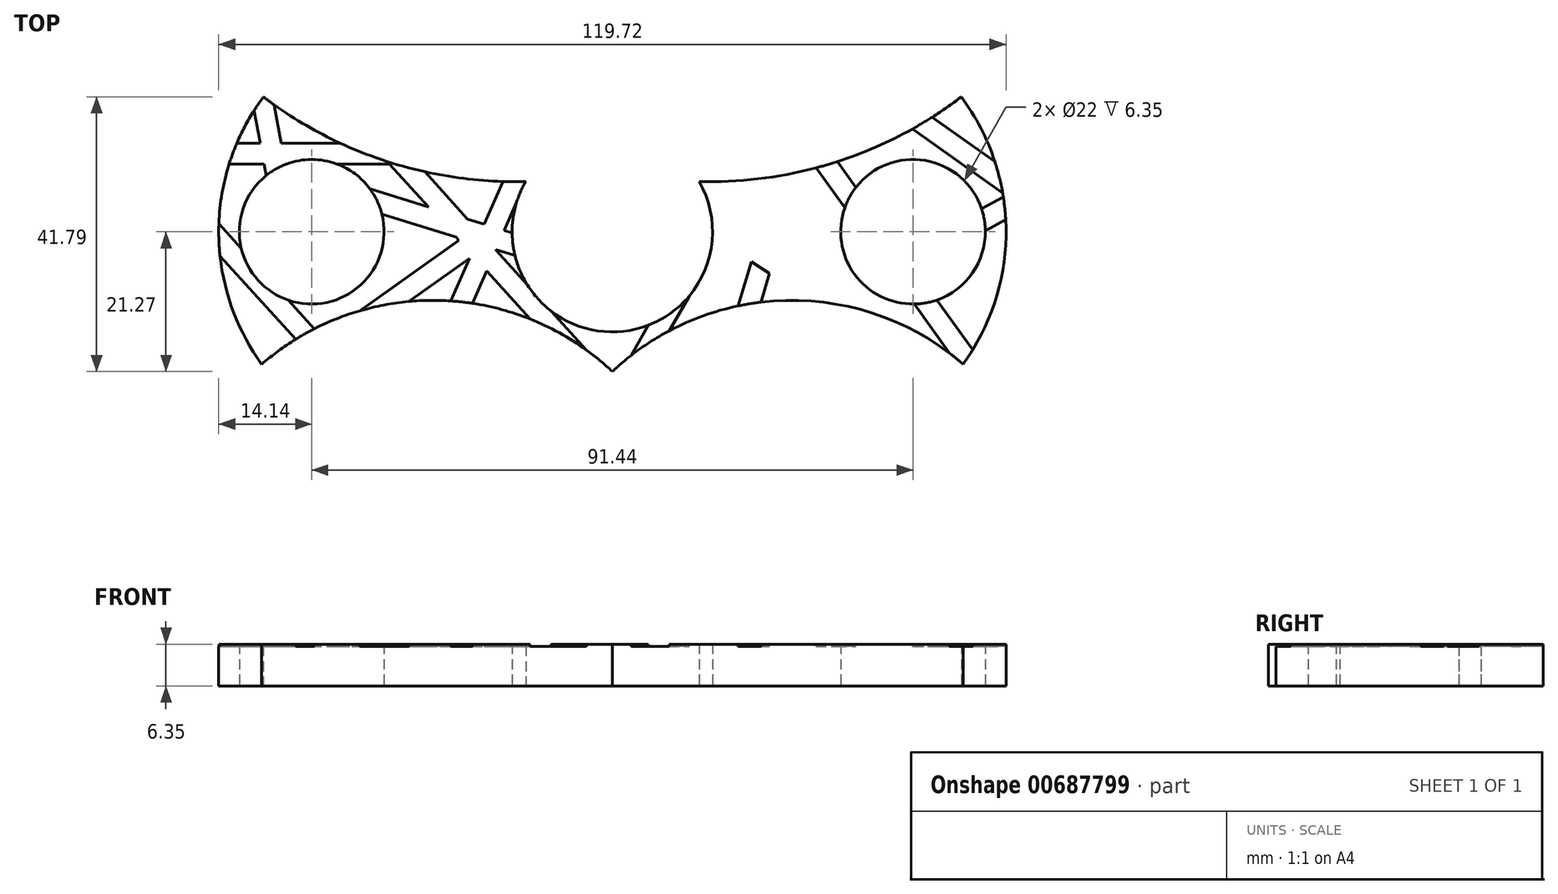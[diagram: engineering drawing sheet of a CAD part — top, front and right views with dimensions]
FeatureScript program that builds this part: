
annotation { "Feature Type Name" : "Feature", "Feature Type Description" : "" }
export const myFeature = defineFeature(function(context is Context, id is Id, definition is map)
    precondition{}
    {
        {
            assignVariable(context, id + "F0", {"name" : "thickness", "anyValue" : 6.35 * mm});
        }
        {
            var Q0;
            Q0=qCreatedBy(makeId("Top.planeOp"),FACE);
            var sketch = newSketch(context, id + "F1", { "sketchPlane" : qUnion([Q0])});
            skCircle(sketch, "E0", {"center": v(0, 0) * mm, "radius": 11 * mm});
            skCircle(sketch, "E1", {"center": v(0, 0) * mm, "radius": 63.5 * mm, "construction": true});
            skCircle(sketch, "E2", {"center": v(0, 0) * mm, "radius": 15.24 * mm});
            skLineSegment(sketch, "E3", {"start": v(0, 0) * mm, "end": v(45.72, 0) * mm, "construction": true});
            skCircle(sketch, "E4", {"center": v(45.72, 0) * mm, "radius": 11 * mm});
            skLineSegment(sketch, "E5", {"start": v(0, 0) * mm, "end": v(-45.72, 0) * mm, "construction": true});
            skCircle(sketch, "E6", {"center": v(-45.72, 0) * mm, "radius": 11 * mm});
            skLineSegment(sketch, "E7", {"start": v(0, -21.27) * mm, "end": v(3.96, -14.72) * mm});
            skLineSegment(sketch, "E8", {"start": v(0, -21.27) * mm, "end": v(-3.96, -14.72) * mm});
            skLineSegment(sketch, "E9", {"start": v(-12.5, 16.99) * mm, "end": v(-8.16, 12.87) * mm});
            skLineSegment(sketch, "E10", {"start": v(-12.5, 16.99) * mm, "end": v(-13.18, 7.66) * mm});
            skLineSegment(sketch, "E11.MirrorCS", {"start": v(12.5, 16.99) * mm, "end": v(13.18, 7.66) * mm});
            skLineSegment(sketch, "E12.MirrorCS", {"start": v(12.5, 16.99) * mm, "end": v(8.16, 12.87) * mm});
            skPoint(sketch, "E13.first.point", {"position": v(-45.72, 18.86) * mm});
            skPoint(sketch, "E13.second.point", {"position": v(-73.63, 0) * mm});
            skPoint(sketch, "E13.third.point", {"position": v(-45.72, -18.86) * mm});
            skLineSegment(sketch, "E14", {"start": v(-51.18, 0) * mm, "end": v(-51.18, -20.99) * mm, "construction": true});
            skArc(sketch, "E15", {"start": v(-53.06, 20.52) * mm, "mid": v(-34.22, 10.68) * mm, "end": v(-13.18, 7.66) * mm});
            skArc(sketch, "E16", {"start": v(-53.06, 20.52) * mm, "mid": v(-59.86, 0.23) * mm, "end": v(-53.32, -20.15) * mm});
            skPoint(sketch, "E16.second.point", {"position": v(-59.86, 0) * mm});
            skPoint(sketch, "E16.third.point", {"position": v(-56.47, -14.88) * mm});
            skArc(sketch, "E17", {"start": v(0, -21.27) * mm, "mid": v(-26.45, -10.45) * mm, "end": v(-53.32, -20.15) * mm});
            skPoint(sketch, "E18.MirrorP", {"position": v(45.72, 18.86) * mm});
            skPoint(sketch, "E19.MirrorP", {"position": v(45.72, -18.86) * mm});
            skLineSegment(sketch, "E20.MirrorCS", {"start": v(51.18, 0) * mm, "end": v(51.18, -20.99) * mm, "construction": true});
            skArc(sketch, "E21.MirrorCS", {"start": v(53.06, 20.52) * mm, "mid": v(59.86, 0.23) * mm, "end": v(53.32, -20.15) * mm});
            skPoint(sketch, "E22.MirrorP", {"position": v(56.47, -14.88) * mm});
            skArc(sketch, "E23.MirrorCS", {"start": v(0, -21.27) * mm, "mid": v(26.45, -10.45) * mm, "end": v(53.32, -20.15) * mm});
            skPoint(sketch, "E24.MirrorP", {"position": v(59.86, 0) * mm});
            skArc(sketch, "E25.MirrorCS", {"start": v(53.06, 20.52) * mm, "mid": v(34.22, 10.68) * mm, "end": v(13.18, 7.66) * mm});
            skSolve(sketch);
        }
        {
            var Q0;
            Q0=makeQuery(id+"F1.imprint","IMPRINT",FACE,{"disambiguationData":[TD([[makeQuery(id+"F1.imprint","IMPRINT",EDGE,{"derivedFrom":sQuery(id+"F1.wireOp",EDGE,"E6")}),-1.0]])]});
            var Q1;
            {var subQ0=sQuery(id+"F1.wireOp",EDGE,"E9");Q1=makeQuery(id+"F1.imprint","IMPRINT",FACE,{"disambiguationData":[TD([[makeQuery(id+"F1.imprint","IMPRINT",EDGE,{"derivedFrom":subQ0}),-1.0]])]});}
            var Q2;
            {var subQ0=sQuery(id+"F1.wireOp",EDGE,"E11.MirrorCS");Q2=makeQuery(id+"F1.imprint","IMPRINT",FACE,{"disambiguationData":[TD([[makeQuery(id+"F1.imprint","IMPRINT",EDGE,{"derivedFrom":subQ0}),-1.0]])]});}
            var Q3;
            {var subQ0=sQuery(id+"F1.wireOp",EDGE,"E7");Q3=makeQuery(id+"F1.imprint","IMPRINT",FACE,{"disambiguationData":[TD([[makeQuery(id+"F1.imprint","IMPRINT",EDGE,{"derivedFrom":subQ0}),1.0]])]});}
            var Q4;
            Q4=makeQuery(id+"F1.imprint","IMPRINT",FACE,{"disambiguationData":[TD([[makeQuery(id+"F1.imprint","IMPRINT",EDGE,{"derivedFrom":sQuery(id+"F1.wireOp",EDGE,"E0")}),1.0]])]});
            var Q5;
            {var subQ1=sQuery(id+"F1.wireOp",EDGE,"E7");Q5=makeQuery(id+"F1.imprint","IMPRINT",FACE,{"disambiguationData":[TD([[makeQuery(id+"F1.imprint","IMPRINT",EDGE,{"derivedFrom":subQ1}),-1.0]])]});}
            extrude(context, id + "F2", {"entities" : qUnion([Q0, Q1, Q2, Q3, Q4, Q5]), "depth" : getVariable(context, 'thickness'), "offsetDistance" : 25.4 * mm});
        }
        {
            var Q0;
            Q0=qCreatedBy(makeId("Top.planeOp"),FACE);
            cPlane(context, id + "F3", {"entities" : qUnion([Q0]), "cplaneType" : CPlaneType.OFFSET, "offset" : getVariable(context, 'thickness') / 2, "width" : 152.4 * mm, "height" : 152.4 * mm});
        }
        {
            var Q0;
            Q0=makeQuery(id+"F2.opExtrude","SWEPT_BODY",BODY,{"disambiguationData":[OSD([sQuery(id+"F1.wireOp",EDGE,"E6"),sQuery(id+"F1.wireOp",EDGE,"E9"),sQuery(id+"F1.wireOp",EDGE,"E10"),sQuery(id+"F1.wireOp",EDGE,"E15"),sQuery(id+"F1.wireOp",EDGE,"E16"),sQuery(id+"F1.wireOp",EDGE,"E17"),sQuery(id+"F1.wireOp",EDGE,"E11.MirrorCS"),sQuery(id+"F1.wireOp",EDGE,"E2"),sQuery(id+"F1.wireOp",EDGE,"E4"),sQuery(id+"F1.wireOp",EDGE,"E12.MirrorCS"),sQuery(id+"F1.wireOp",EDGE,"E21.MirrorCS"),sQuery(id+"F1.wireOp",EDGE,"E0"),sQuery(id+"F1.wireOp",EDGE,"E23.MirrorCS"),sQuery(id+"F1.wireOp",EDGE,"E25.MirrorCS")])]});
            var Q1;
            Q1=qCreatedBy(id+"F3.planeOp",FACE);
            mirror(context, id + "F4", {"operationType" : NewBodyOperationType.INTERSECT, "entities" : qUnion([Q0]), "mirrorPlane" : qUnion([Q1])});
        }
        {
            var Q0;
            Q0=makeQuery(id+"F2.opExtrude","CAP_FACE",FACE,{"disambiguationData":[OSD([sQuery(id+"F1.wireOp",EDGE,"E6"),sQuery(id+"F1.wireOp",EDGE,"E9"),sQuery(id+"F1.wireOp",EDGE,"E10"),sQuery(id+"F1.wireOp",EDGE,"E15"),sQuery(id+"F1.wireOp",EDGE,"E16"),sQuery(id+"F1.wireOp",EDGE,"E17"),sQuery(id+"F1.wireOp",EDGE,"E11.MirrorCS"),sQuery(id+"F1.wireOp",EDGE,"E2"),sQuery(id+"F1.wireOp",EDGE,"E4"),sQuery(id+"F1.wireOp",EDGE,"E12.MirrorCS"),sQuery(id+"F1.wireOp",EDGE,"E21.MirrorCS"),sQuery(id+"F1.wireOp",EDGE,"E0"),sQuery(id+"F1.wireOp",EDGE,"E23.MirrorCS"),sQuery(id+"F1.wireOp",EDGE,"E25.MirrorCS")])],"isStart":false});
            var sketch = newSketch(context, id + "F5", { "sketchPlane" : qUnion([Q0])});
            skLineSegment(sketch, "E26", {"start": v(-54.49, 18.45) * mm, "end": v(-53.56, 13.5) * mm});
            skLineSegment(sketch, "E27", {"start": v(-51.42, 19.31) * mm, "end": v(-50.33, 13.5) * mm});
            skLineSegment(sketch, "E28", {"start": v(-34.22, 10.68) * mm, "end": v(-27.97, 3.78) * mm});
            skLineSegment(sketch, "E29", {"start": v(-28.53, 9.14) * mm, "end": v(-22, 1.93) * mm});
            skLineSegment(sketch, "E30", {"start": v(-23.36, -1.3) * mm, "end": v(-38.4, -12.02) * mm});
            skLineSegment(sketch, "E31", {"start": v(-21.21, -3.67) * mm, "end": v(-30.94, -10.6) * mm});
            skLineSegment(sketch, "E32", {"start": v(-59.83, 1.25) * mm, "end": v(-45.32, -14.77) * mm});
            skLineSegment(sketch, "E33", {"start": v(-59.66, -3.67) * mm, "end": v(-48.16, -16.36) * mm});
            skLineSegment(sketch, "E34", {"start": v(-36.88, 6.55) * mm, "end": v(-27.97, 3.78) * mm});
            skLineSegment(sketch, "E35", {"start": v(-35.05, 2.65) * mm, "end": v(-23.78, -0.84) * mm});
            skLineSegment(sketch, "E36", {"start": v(2.86, -18.82) * mm, "end": v(10.74, -5.02) * mm});
            skLineSegment(sketch, "E37", {"start": v(21.84, 8.02) * mm, "end": v(17.94, 1.2) * mm});
            skLineSegment(sketch, "E38", {"start": v(10.83, 1.94) * mm, "end": v(13.68, 0.13) * mm});
            skLineSegment(sketch, "E39", {"start": v(39.33, -12.3) * mm, "end": v(36.89, -10.76) * mm});
            skLineSegment(sketch, "E40", {"start": v(10.86, -1.77) * mm, "end": v(12.8, -1.42) * mm});
            skLineSegment(sketch, "E41", {"start": v(9.69, -5.22) * mm, "end": v(10.74, -5.02) * mm});
            skLineSegment(sketch, "E42", {"start": v(48.62, 17.43) * mm, "end": v(58.15, 10.68) * mm});
            skPoint(sketch, "E42.endSnap0", {"position": v(34.22, 10.68) * mm});
            skLineSegment(sketch, "E43", {"start": v(45.64, 15.66) * mm, "end": v(59.34, 5.95) * mm});
            skLineSegment(sketch, "E44", {"start": v(30.99, 9.73) * mm, "end": v(41.35, -4.68) * mm});
            skLineSegment(sketch, "E45", {"start": v(34.22, 10.68) * mm, "end": v(44.15, -3.14) * mm});
            skLineSegment(sketch, "E46", {"start": v(-57.1, 13.5) * mm, "end": v(-53.56, 13.5) * mm});
            skPoint(sketch, "E46.startSnap0", {"position": v(-53.56, 13.5) * mm});
            skLineSegment(sketch, "E47", {"start": v(-58.27, 10.33) * mm, "end": v(-52.96, 10.33) * mm});
            skLineSegment(sketch, "E48", {"start": v(59.45, 5.3) * mm, "end": v(44.15, -3.14) * mm});
            skLineSegment(sketch, "E49", {"start": v(59.8, 1.88) * mm, "end": v(46.01, -5.73) * mm});
            skLineSegment(sketch, "E50", {"start": v(-34.42, -33.18) * mm, "end": v(-21.46, -3.4) * mm});
            skLineSegment(sketch, "E51", {"start": v(-31.26, -33.87) * mm, "end": v(-19.12, -5.99) * mm});
            skLineSegment(sketch, "E52.trimOffspring", {"start": v(-50.33, 13.5) * mm, "end": v(-41.42, 13.5) * mm});
            skLineSegment(sketch, "E53.trimOffspring", {"start": v(-52.96, 10.33) * mm, "end": v(-52.63, 8.56) * mm});
            skLineSegment(sketch, "E54.trimOffspring", {"start": v(-49.73, 10.33) * mm, "end": v(-49.72, 10.25) * mm});
            skLineSegment(sketch, "E55.trimOffspring", {"start": v(-49.73, 10.33) * mm, "end": v(-33.09, 10.33) * mm});
            skLineSegment(sketch, "E56.trimOffspring", {"start": v(-22, 1.93) * mm, "end": v(-19.47, 1.15) * mm});
            skLineSegment(sketch, "E57.trimOffspring", {"start": v(-23.78, -0.84) * mm, "end": v(-23.36, -1.3) * mm});
            skLineSegment(sketch, "E58.trimOffspring", {"start": v(-17.82, -2.7) * mm, "end": v(-3.94, -18.01) * mm});
            skLineSegment(sketch, "E59.trimOffspring", {"start": v(-19.47, 1.15) * mm, "end": v(-16.64, 7.66) * mm});
            skLineSegment(sketch, "E60.trimOffspring", {"start": v(-17.82, -2.7) * mm, "end": v(-9.69, -5.21) * mm});
            skLineSegment(sketch, "E61.trimOffspring", {"start": v(-21.46, -3.4) * mm, "end": v(-21.21, -3.67) * mm});
            skLineSegment(sketch, "E62.trimOffspring", {"start": v(-19.12, -5.99) * mm, "end": v(-12.5, -13.28) * mm});
            skLineSegment(sketch, "E63.trimOffspring", {"start": v(-17.73, -2.8) * mm, "end": v(-17.7, -2.73) * mm});
            skLineSegment(sketch, "E64.trimOffspring", {"start": v(-16.42, 0.2) * mm, "end": v(-10.9, -1.51) * mm});
            skLineSegment(sketch, "E65.trimOffspring", {"start": v(-16.42, 0.2) * mm, "end": v(-13.18, 7.66) * mm});
            skLineSegment(sketch, "E66.trimOffspring", {"start": v(15.26, 2.9) * mm, "end": v(8.16, 7.38) * mm});
            skLineSegment(sketch, "E67.trimOffspring", {"start": v(15.26, 2.9) * mm, "end": v(18, 7.71) * mm});
            skLineSegment(sketch, "E68.trimOffspring", {"start": v(14.82, -4.28) * mm, "end": v(8.66, -15.07) * mm});
            skLineSegment(sketch, "E69.trimOffspring", {"start": v(20, -0.1) * mm, "end": v(22.58, 0.37) * mm});
            skLineSegment(sketch, "E70.trimOffspring", {"start": v(19.35, -3.45) * mm, "end": v(30.65, -10.58) * mm});
            skLineSegment(sketch, "E71.trimOffspring", {"start": v(12.8, -1.42) * mm, "end": v(13.68, 0.13) * mm});
            skLineSegment(sketch, "E72.trimOffspring", {"start": v(20, -0.1) * mm, "end": v(17.94, 1.2) * mm});
            skLineSegment(sketch, "E73.trimOffspring", {"start": v(25.07, -2.4) * mm, "end": v(34.74, -0.63) * mm});
            skLineSegment(sketch, "E74.trimOffspring", {"start": v(14.82, -4.28) * mm, "end": v(19.35, -3.45) * mm});
            skLineSegment(sketch, "E75.trimOffspring", {"start": v(41.35, -4.68) * mm, "end": v(33.82, -8.83) * mm});
            skLineSegment(sketch, "E76.trimOffspring", {"start": v(43.21, -7.28) * mm, "end": v(35.8, -11.36) * mm});
            skLineSegment(sketch, "E77.trimOffspring", {"start": v(43.21, -7.28) * mm, "end": v(51.27, -18.5) * mm});
            skLineSegment(sketch, "E78.trimOffspring", {"start": v(46.01, -5.73) * mm, "end": v(54.8, -17.95) * mm});
            skLineSegment(sketch, "E79.trimOffspring", {"start": v(33.82, -8.83) * mm, "end": v(24.84, -3.16) * mm});
            skLineSegment(sketch, "E80", {"start": v(24.97, 8.45) * mm, "end": v(22.58, 0.37) * mm});
            skLineSegment(sketch, "E81", {"start": v(28.49, 9.13) * mm, "end": v(26.08, 1.01) * mm});
            skLineSegment(sketch, "E82.trimOffspring", {"start": v(26.08, 1.01) * mm, "end": v(35.05, 2.65) * mm});
            skLineSegment(sketch, "E83.trimOffspring", {"start": v(21.11, -4.56) * mm, "end": v(19.12, -11.28) * mm});
            skLineSegment(sketch, "E84.trimOffspring", {"start": v(25.07, -2.4) * mm, "end": v(24.84, -3.16) * mm});
            skLineSegment(sketch, "E85.trimOffspring", {"start": v(23.9, -6.32) * mm, "end": v(22.6, -10.71) * mm});
            skSolve(sketch);
        }
        {
            var Q0;
            Q0 = qSketchRegion(id + "F5", true);
            var Q1;
            {var subQ11=sQuery(id+"F5.wireOp",EDGE,"E26");Q1=makeQuery(id+"F5.imprint","IMPRINT",FACE,{"disambiguationData":[TD([[makeQuery(id+"F5.imprint","IMPRINT",EDGE,{"derivedFrom":subQ11}),1.0]])]});}
            var Q2;
            {var subQ3=sQuery(id+"F5.wireOp",EDGE,"E33");Q2=makeQuery(id+"F5.imprint","IMPRINT",FACE,{"disambiguationData":[TD([[makeQuery(id+"F5.imprint","IMPRINT",EDGE,{"derivedFrom":subQ3}),1.0]])]});}
            var Q3;
            {var subQ11=sQuery(id+"F5.wireOp",EDGE,"E29");Q3=makeQuery(id+"F5.imprint","IMPRINT",FACE,{"disambiguationData":[TD([[makeQuery(id+"F5.imprint","IMPRINT",EDGE,{"derivedFrom":subQ11}),-1.0]])]});}
            var Q4;
            {var subQ17=sQuery(id+"F5.wireOp",EDGE,"E36");Q4=makeQuery(id+"F5.imprint","IMPRINT",FACE,{"disambiguationData":[TD([[makeQuery(id+"F5.imprint","IMPRINT",EDGE,{"derivedFrom":subQ17}),-1.0]])]});}
            var Q5;
            {var subQ0=sQuery(id+"F5.wireOp",EDGE,"E44");var subQ1=makeQuery(id+"F2.opExtrude","CAP_EDGE",EDGE,{"disambiguationData":[OSD([sQuery(id+"F1.wireOp",EDGE,"E25.MirrorCS")])],"isStart":false});var subQ2=makeQuery(id+"F5.imprint","INTERSECT",VERTEX,{"derivedFrom":[subQ1,subQ0]});Q5=makeQuery(id+"F5.imprint","IMPRINT",FACE,{"disambiguationData":[TD([[makeQuery(id+"F5.imprint","IMPRINT",EDGE,{"disambiguationData":[TD([[subQ2,-1.0]])],"derivedFrom":subQ0}),1.0]])]});}
            var Q6;
            {var subQ0=makeQuery(id+"F2.opExtrude","CAP_EDGE",EDGE,{"disambiguationData":[OSD([sQuery(id+"F1.wireOp",EDGE,"E23.MirrorCS")])],"isStart":false});var subQ3=sQuery(id+"F5.wireOp",EDGE,"E77.trimOffspring");var subQ4=makeQuery(id+"F5.imprint","INTERSECT",VERTEX,{"derivedFrom":[subQ0,subQ3]});Q6=makeQuery(id+"F5.imprint","IMPRINT",FACE,{"disambiguationData":[TD([[makeQuery(id+"F5.imprint","IMPRINT",EDGE,{"disambiguationData":[TD([[subQ4,1.0]])],"derivedFrom":subQ3}),1.0]])]});}
            var Q7;
            {var subQ0=sQuery(id+"F5.wireOp",EDGE,"E48");var subQ1=makeQuery(id+"F2.opExtrude","CAP_EDGE",EDGE,{"disambiguationData":[OSD([sQuery(id+"F1.wireOp",EDGE,"E21.MirrorCS")])],"isStart":false});var subQ2=makeQuery(id+"F5.imprint","INTERSECT",VERTEX,{"derivedFrom":[subQ1,subQ0]});Q7=makeQuery(id+"F5.imprint","IMPRINT",FACE,{"disambiguationData":[TD([[makeQuery(id+"F5.imprint","IMPRINT",EDGE,{"disambiguationData":[TD([[subQ2,-1.0]])],"derivedFrom":subQ0}),1.0]])]});}
            var Q8;
            {var subQ0=sQuery(id+"F5.wireOp",EDGE,"E42");Q8=makeQuery(id+"F5.imprint","IMPRINT",FACE,{"disambiguationData":[TD([[makeQuery(id+"F5.imprint","IMPRINT",EDGE,{"derivedFrom":subQ0}),-1.0]])]});}
            var Q9;
            {var subQ0=sQuery(id+"F5.wireOp",EDGE,"E28");var subQ1=makeQuery(id+"F2.opExtrude","CAP_EDGE",EDGE,{"disambiguationData":[OSD([sQuery(id+"F1.wireOp",EDGE,"E15")])],"isStart":false});var subQ2=makeQuery(id+"F5.imprint","INTERSECT",VERTEX,{"derivedFrom":[subQ1,subQ0]});Q9=makeQuery(id+"F5.imprint","IMPRINT",FACE,{"disambiguationData":[TD([[makeQuery(id+"F5.imprint","IMPRINT",EDGE,{"disambiguationData":[TD([[subQ2,-1.0]])],"derivedFrom":subQ0}),1.0]])]});}
            var Q10;
            {var subQ0=sQuery(id+"F5.wireOp",EDGE,"E83.trimOffspring");Q10=makeQuery(id+"F5.imprint","IMPRINT",FACE,{"disambiguationData":[TD([[makeQuery(id+"F5.imprint","IMPRINT",EDGE,{"derivedFrom":subQ0}),1.0]])]});}
            extrude(context, id + "F6", {"entities" : qUnion([Q0, Q1, Q2, Q3, Q4, Q5, Q6, Q7, Q8, Q9, Q10]), "operationType" : NewBodyOperationType.REMOVE, "oppositeDirection" : true, "depth" : getVariable(context, 'thickness') / 20, "offsetDistance" : 25.4 * mm});
        }
    });
